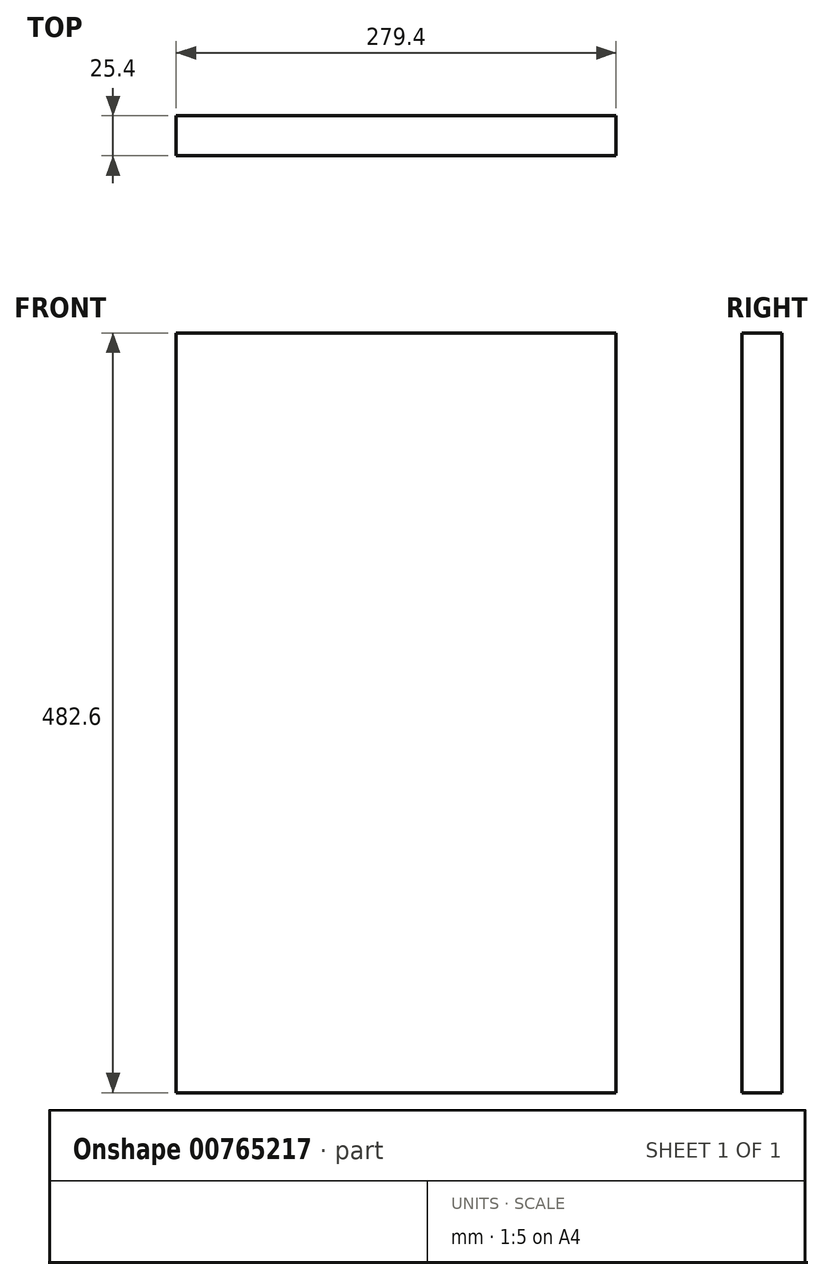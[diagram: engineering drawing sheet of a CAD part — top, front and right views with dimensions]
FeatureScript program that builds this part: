
annotation { "Feature Type Name" : "Feature", "Feature Type Description" : "" }
export const myFeature = defineFeature(function(context is Context, id is Id, definition is map)
    precondition{}
    {
        {
            var Q0;
            Q0=qCreatedBy(makeId("Front.planeOp"),FACE);
            var sketch = newSketch(context, id + "F0", { "sketchPlane" : qUnion([Q0])});
            skLineSegment(sketch, "E0.bottom", {"start": v(-278.92, 60.09) * mm, "end": v(0.48, 60.09) * mm});
            skLineSegment(sketch, "E0.top", {"start": v(-278.92, -422.51) * mm, "end": v(0.48, -422.51) * mm});
            skLineSegment(sketch, "E0.left", {"start": v(-278.92, 60.09) * mm, "end": v(-278.92, -422.51) * mm});
            skLineSegment(sketch, "E0.right", {"start": v(0.48, 60.09) * mm, "end": v(0.48, -422.51) * mm});
            skSolve(sketch);
        }
        {
            var Q0;
            Q0=makeQuery(id+"F0.imprint","IMPRINT",FACE,{"disambiguationData":[TD([[makeQuery(id+"F0.imprint","IMPRINT",EDGE,{"derivedFrom":sQuery(id+"F0.wireOp",EDGE,"E0.bottom")}),-1.0]])]});
            extrude(context, id + "F1", {"entities" : qUnion([Q0]), "depth" : 25.4 * mm, "offsetDistance" : 25.4 * mm});
        }
    });
